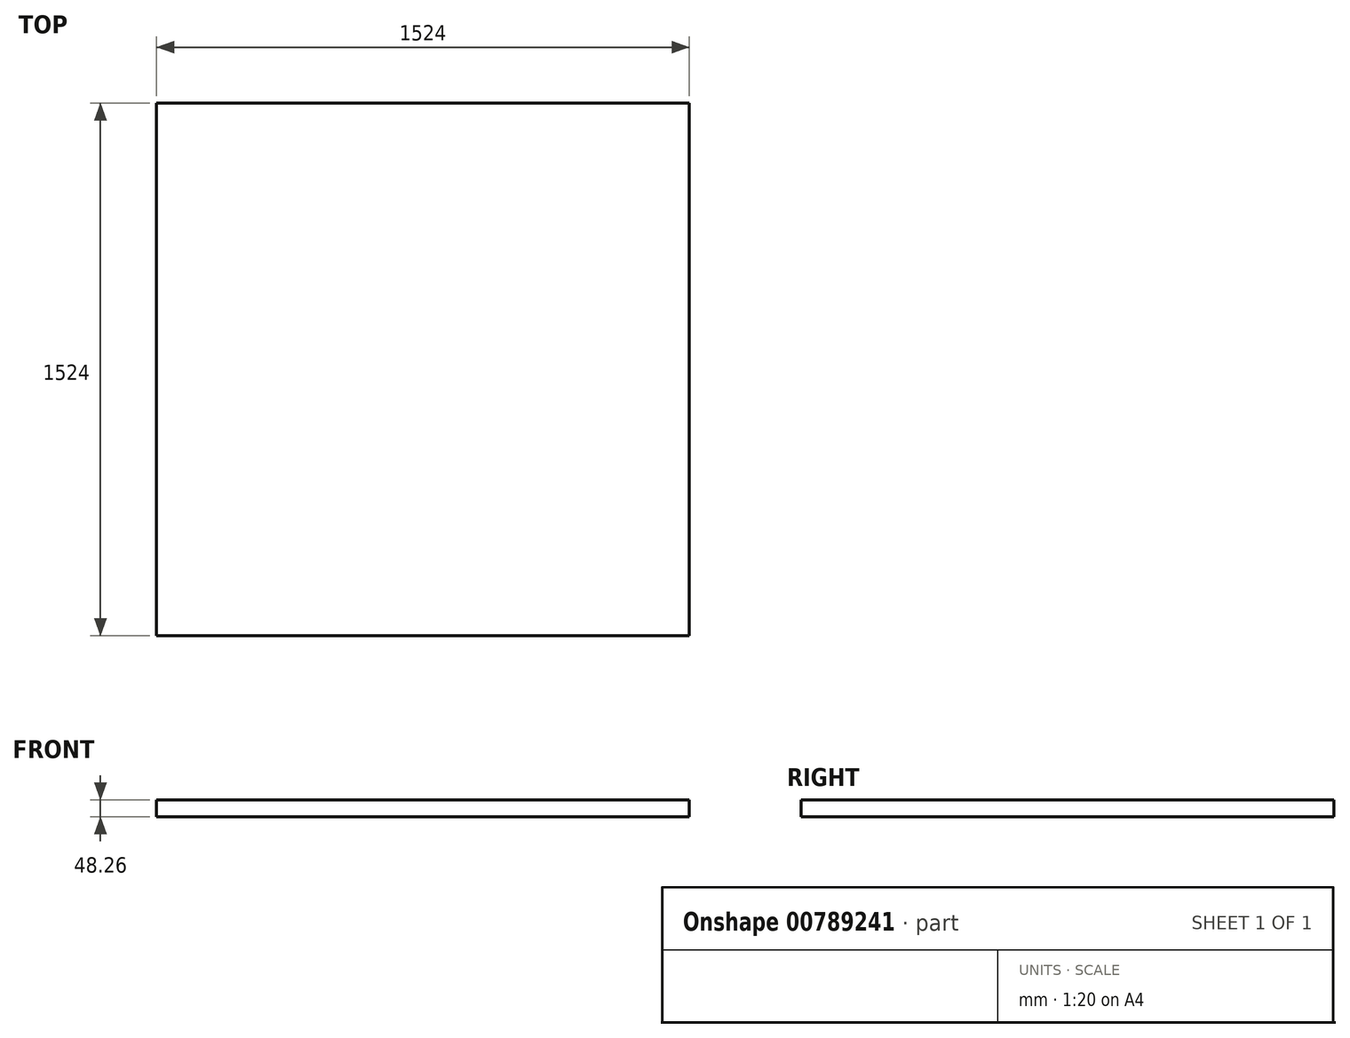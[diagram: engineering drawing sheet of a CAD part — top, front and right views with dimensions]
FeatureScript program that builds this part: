
annotation { "Feature Type Name" : "Feature", "Feature Type Description" : "" }
export const myFeature = defineFeature(function(context is Context, id is Id, definition is map)
    precondition{}
    {
        {
            var Q0;
            Q0=qCreatedBy(makeId("Front.planeOp"),FACE);
            var sketch = newSketch(context, id + "F0", { "sketchPlane" : qUnion([Q0])});
            skLineSegment(sketch, "E0.bottom", {"start": v(0, 0) * mm, "end": v(1524, 0) * mm});
            skLineSegment(sketch, "E0.top", {"start": v(0, 48.26) * mm, "end": v(1524, 48.26) * mm});
            skLineSegment(sketch, "E0.left", {"start": v(0, 0) * mm, "end": v(0, 48.26) * mm});
            skLineSegment(sketch, "E0.right", {"start": v(1524, 0) * mm, "end": v(1524, 48.26) * mm});
            skSolve(sketch);
        }
        {
            var Q0;
            Q0 = qSketchRegion(id + "F0", true);
            extrude(context, id + "F1", {"entities" : qUnion([Q0]), "depth" : 1524 * mm, "offsetDistance" : 25.4 * mm});
        }
    });
